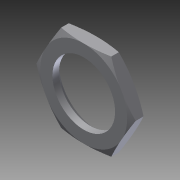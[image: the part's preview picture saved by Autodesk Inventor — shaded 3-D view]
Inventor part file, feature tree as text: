
AUTODESK INVENTOR PART (.ipt)
format: ipt  version: 2014 (Build 180170000, 170)  size: 130,560 bytes
history: native  units: in
note: dims shown in document units (in); Inventor stores cm internally (conversion verified against a paired STEP export)
features: other x7, sketch x3, revolve x1, extrude x1, hole x1
ambient origin geometry x8: Origin, YZ Plane, XZ Plane, XY Plane, X Axis, Y Axis, Z Axis, Center Point
bodies: Solid1 (feature_tree)
feature tree (13):
  revolve  "Revolution1"  [1 undecoded]
  extrude  "Extrusion1"  [1 undecoded]
  hole  "Drilling 1"  [1 undecoded]
  other  "nut_XY"
  other  "nut_YZ"
  other  "nut_ZX"
  other  "nut_X"
  other  "nut_Y"
  other  "nut_Z"
  other  "nut_Center"
  sketch  "Sketch_1"  dims[d0=360.0deg d1=0.158in d2=0.0in]
  sketch  "Sketch_2"  dims[d3=0.3979in d4=0.75in d5=0.472in d6=0.25in d7=0.6184in d8=0.079in d9=0.0in]
  sketch  "Sketch3"
note: 3 required parameter values undecoded (feature->parameter linkage not recoverable at this tier; creation-order binding heuristic only, values carry confidence <= 0.55)